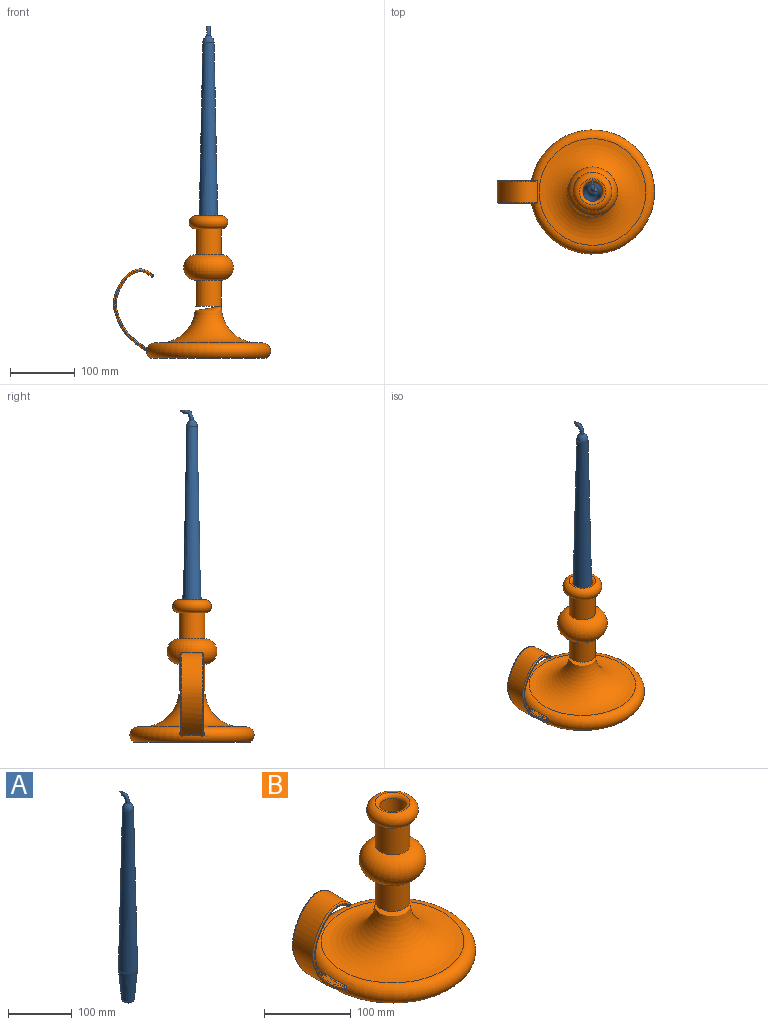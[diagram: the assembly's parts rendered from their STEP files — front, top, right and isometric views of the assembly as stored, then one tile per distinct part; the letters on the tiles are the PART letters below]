
ASSEMBLY  parts=2 mates=1
PART A: 10 faces, bbox 32.5x34.3x393.9 mm
  f0: revolved ~17.35x17.35mm, area 534.3mm2, adj f3,f4
  f1: plane 10.39x10.39mm, normal (0,0,-1), area 84.7mm2, adj f7
  f2: cone r=9.87mm half-angle=4.7deg, axis (0,0,1), area 4522.4mm2, adj f7,f8
  f3: cone r=15mm half-angle=1.2deg, axis (0,0,-1), area 22728.5mm2, adj f0,f8
  f4: bspline ~15.84x13.8mm, area 348.8mm2, adj f0,f6
  f5: plane 0.16x0.13mm, normal (0,0.96,0.27), area 0mm2, adj f9
  f6: bspline ~6.69x5.74mm, area 72.9mm2, adj f4,f9
  f7: torus R=5.19mm, axis (0,0,1), area 395.4mm2, adj f1,f2
  f8: torus R=9.92mm, axis (0,0,-1), area 49.5mm2, adj f2,f3
  f9: bspline ~0.86x0.85mm, area 0.8mm2, adj f5,f6
PART B: 32 faces, bbox 274.6x254.6x220 mm
  f0: torus R=83.57mm, axis (0,0,1), area 19168.1mm2, adj f1,f2,f17,f21,f22,f25,f26,f28
  f1: plane 180x180mm, normal (0,0,-1), area 25446.9mm2, adj f0
  f2: torus R=77.08mm, axis (0,0,1), area 25693.2mm2, adj f0,f3
  f3: cylinder r=20mm len=40.1mm, axis (0,0,1), area 5038.5mm2, adj f2,f4
  f4: torus R=18.62mm, axis (0,0,1), area 12044.2mm2, adj f3,f5
  f5: cylinder r=20mm len=40mm, axis (0,0,1), area 5026.5mm2, adj f4,f6
  f6: torus R=20mm, axis (0,0,1), area 5184mm2, adj f5,f31
  f7: cylinder r=15mm len=95mm, axis (0,0,1), area 8953.1mm2, adj f8,f31
  f8: plane 30x30mm, normal (0,0,1), area 706.9mm2, adj f7
  f9: bspline ~121.74x55.49mm, area 5457.9mm2, adj f20,f24,f27,f30
  f10: bspline ~130.06x62.94mm, area 6013.8mm2, adj f14,f16,f17,f18
  f11: plane 123.39x59.66mm, normal (0,1,0), area 142.6mm2, adj f13,f14,f16,f24,f25
  f12: plane 123.39x58.38mm, normal (0,-1,0), area 141.6mm2, adj f18,f19,f26,f27
  f13: plane 33.47x0.56mm, normal (0.7,0,-0.71), area 26.2mm2, adj f11,f14,f19,f20,f24
  f14: cylinder r=1.78mm len=33.47mm, axis (0,-1,0), area 93.8mm2, adj f10,f11,f13,f15,f16
  f15: sphere r=1.78mm, area 4.4mm2, adj f14,f18,f19
  f16: bspline ~127.66x63.7mm, area 524.7mm2, adj f10,f11,f14,f21
  f17: bspline ~40.95x3.19mm, area 53.9mm2, adj f0,f10,f21,f22
  f18: bspline ~128.27x63.28mm, area 522.1mm2, adj f10,f12,f15,f22
  f19: cylinder r=1.78mm len=1.82mm, axis (0.71,0,0.7), area 2.2mm2, adj f12,f13,f15,f23
  f20: cylinder r=1.78mm len=33.47mm, axis (0,1,0), area 88.9mm2, adj f9,f13,f23,f24
  f21: bspline ~4.17x3.84mm, area 7.8mm2, adj f0,f16,f17,f25
  f22: bspline ~4.04x3.88mm, area 7.8mm2, adj f0,f17,f18,f26
  f23: sphere r=1.78mm, area 5.5mm2, adj f19,f20,f27
  f24: bspline ~122.71x58.8mm, area 491.8mm2, adj f9,f11,f13,f20,f28
  f25: bspline ~1.97x1.77mm, area 1.9mm2, adj f0,f11,f21,f28
  f26: bspline ~3.05x2.22mm, area 1.9mm2, adj f0,f12,f22,f29
  f27: bspline ~122.71x58.16mm, area 488.9mm2, adj f9,f12,f23,f29
  f28: bspline ~3.67x3.49mm, area 10.3mm2, adj f0,f24,f25,f30
  f29: bspline ~4.26x3.9mm, area 10.3mm2, adj f0,f26,f27,f30
  f30: bspline ~36.95x3.86mm, area 89.9mm2, adj f0,f9,f28,f29
  f31: torus R=20.08mm, axis (0,0,-1), area 855.1mm2, adj f6,f7
PLACE A t=(59.46,179.54,66.97)mm
PLACE B t=(59.46,179.54,-140.51)mm
MATE fastened B.f7 <-> A.f2  axis (0,0,1) through (59.46,179.54,-124.44)mm
